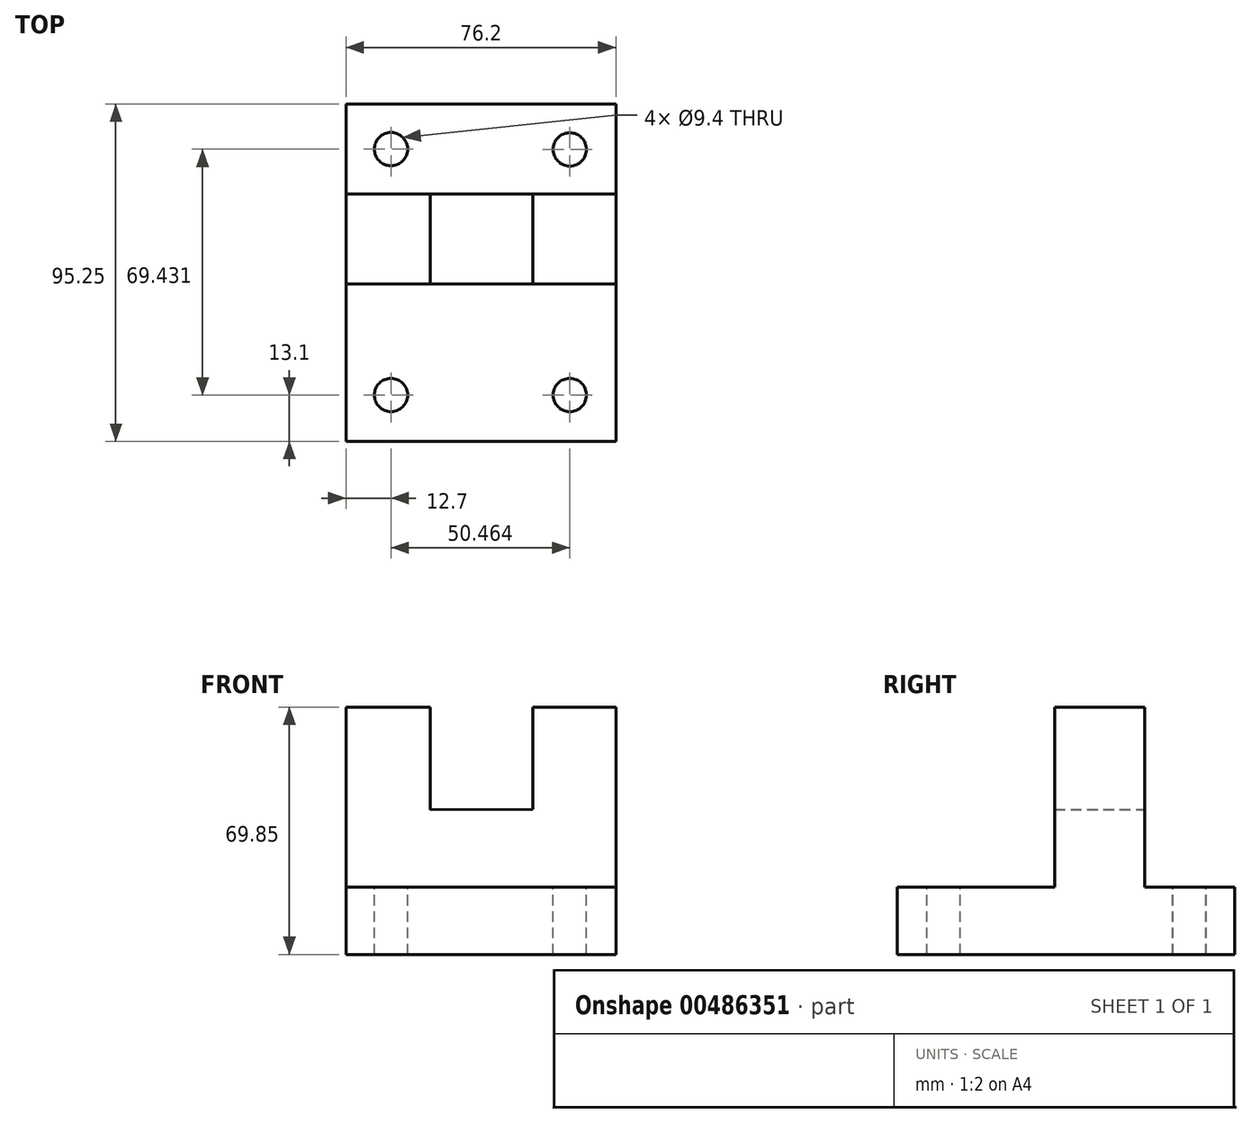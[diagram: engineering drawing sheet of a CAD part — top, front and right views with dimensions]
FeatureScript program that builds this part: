
annotation { "Feature Type Name" : "Feature", "Feature Type Description" : "" }
export const myFeature = defineFeature(function(context is Context, id is Id, definition is map)
    precondition{}
    {
        {
            var Q0;
            Q0=qCreatedBy(makeId("Right.planeOp"),FACE);
            var sketch = newSketch(context, id + "F0", { "sketchPlane" : qUnion([Q0])});
            skLineSegment(sketch, "E0", {"start": v(40.84, -32.67) * mm, "end": v(-54.41, -32.67) * mm});
            skLineSegment(sketch, "E1", {"start": v(40.84, -32.67) * mm, "end": v(40.84, -13.62) * mm});
            skLineSegment(sketch, "E2", {"start": v(-54.41, -32.67) * mm, "end": v(-54.41, -13.62) * mm});
            skLineSegment(sketch, "E3", {"start": v(-54.41, -13.62) * mm, "end": v(-9.96, -13.62) * mm});
            skLineSegment(sketch, "E4", {"start": v(-9.96, -13.62) * mm, "end": v(-9.96, 37.18) * mm});
            skLineSegment(sketch, "E5", {"start": v(-9.96, 37.18) * mm, "end": v(15.44, 37.18) * mm});
            skLineSegment(sketch, "E6", {"start": v(40.84, -13.62) * mm, "end": v(15.44, -13.62) * mm});
            skLineSegment(sketch, "E7", {"start": v(15.44, -13.62) * mm, "end": v(15.44, 37.18) * mm});
            skSolve(sketch);
        }
        {
            var Q0;
            Q0=makeQuery(id+"F0.imprint","IMPRINT",FACE,{"disambiguationData":[TD([[makeQuery(id+"F0.imprint","IMPRINT",EDGE,{"derivedFrom":sQuery(id+"F0.wireOp",EDGE,"E0")}),-1.0]])]});
            extrude(context, id + "F1", {"entities" : qUnion([Q0]), "depth" : 76.2 * mm, "offsetDistance" : 25.4 * mm});
        }
        {
            var Q0;
            Q0=qCreatedBy(makeId("Front.planeOp"),FACE);
            var sketch = newSketch(context, id + "F2", { "sketchPlane" : qUnion([Q0])});
            skLineSegment(sketch, "E8", {"start": v(52.71, 36.94) * mm, "end": v(52.71, 8.36) * mm});
            skLineSegment(sketch, "E9", {"start": v(23.83, 36.77) * mm, "end": v(23.83, 8.2) * mm});
            skLineSegment(sketch, "E10", {"start": v(23.83, 8.2) * mm, "end": v(52.71, 8.36) * mm});
            skPoint(sketch, "E11.start.orphan", {"position": v(0, 36.77) * mm});
            skLineSegment(sketch, "E12", {"start": v(23.83, 36.77) * mm, "end": v(23.83, 49.71) * mm});
            skLineSegment(sketch, "E13", {"start": v(23.83, 49.71) * mm, "end": v(52.71, 49.71) * mm});
            skLineSegment(sketch, "E14", {"start": v(52.71, 49.71) * mm, "end": v(52.71, 36.94) * mm});
            skSolve(sketch);
        }
        {
            var Q0;
            Q0=makeQuery(id+"F2.imprint","IMPRINT",FACE,{"disambiguationData":[TD([[makeQuery(id+"F2.imprint","IMPRINT",EDGE,{"derivedFrom":sQuery(id+"F2.wireOp",EDGE,"E8")}),-1.0]])]});
            var Q1;
            Q1=makeQuery(id+"F2.imprint","IMPRINT",FACE,{"disambiguationData":[TD([[makeQuery(id+"F2.imprint","IMPRINT",EDGE,{"derivedFrom":sQuery(id+"F2.wireOp",EDGE,"E8")}),-1.0]])]});
            extrude(context, id + "F3", {"entities" : qUnion([Q0, Q1]), "operationType" : NewBodyOperationType.REMOVE, "endBound" : BoundingType.THROUGH_ALL, "depth" : 25.4 * mm, "offsetDistance" : 25.4 * mm, "hasSecondDirection" : true, "secondDirectionOppositeDirection" : true, "secondDirectionDepth" : 50.8 * mm});
        }
        {
            var Q0;
            Q0=qCreatedBy(makeId("Top.planeOp"),FACE);
            var sketch = newSketch(context, id + "F4", { "sketchPlane" : qUnion([Q0])});
            skCircle(sketch, "E15", {"center": v(63.16, -41.31) * mm, "radius": 4.7 * mm});
            skPoint(sketch, "E16.end.orphan", {"position": v(75.86, -41.31) * mm});
            skPoint(sketch, "E17.end.orphan", {"position": v(63.16, -54.01) * mm});
            skCircle(sketch, "E18", {"center": v(12.7, -41.31) * mm, "radius": 4.7 * mm});
            skPoint(sketch, "E19.end.orphan", {"position": v(0, -41.31) * mm});
            skPoint(sketch, "E20.end.orphan", {"position": v(12.7, -54.01) * mm});
            skPoint(sketch, "E20.start.orphan", {"position": v(0, -54.01) * mm});
            skLineSegment(sketch, "E21", {"start": v(0, 40.82) * mm, "end": v(0, 28.12) * mm});
            skCircle(sketch, "E22", {"center": v(12.7, 28.12) * mm, "radius": 4.7 * mm});
            skPoint(sketch, "E23.start.orphan", {"position": v(12.7, 40.82) * mm});
            skLineSegment(sketch, "E24", {"start": v(76.2, 40.74) * mm, "end": v(76.2, 28.04) * mm});
            skCircle(sketch, "E25", {"center": v(63.16, 28.04) * mm, "radius": 4.7 * mm});
            skSolve(sketch);
        }
        {
            var Q0;
            Q0=makeQuery(id+"F4.imprint","IMPRINT",FACE,{"disambiguationData":[TD([[makeQuery(id+"F4.imprint","IMPRINT",EDGE,{"derivedFrom":sQuery(id+"F4.wireOp",EDGE,"E22")}),1.0]])]});
            var Q1;
            Q1=makeQuery(id+"F4.imprint","IMPRINT",FACE,{"disambiguationData":[TD([[makeQuery(id+"F4.imprint","IMPRINT",EDGE,{"derivedFrom":sQuery(id+"F4.wireOp",EDGE,"E25")}),1.0]])]});
            var Q2;
            Q2=makeQuery(id+"F4.imprint","IMPRINT",FACE,{"disambiguationData":[TD([[makeQuery(id+"F4.imprint","IMPRINT",EDGE,{"derivedFrom":sQuery(id+"F4.wireOp",EDGE,"E15")}),1.0]])]});
            var Q3;
            Q3=makeQuery(id+"F4.imprint","IMPRINT",FACE,{"disambiguationData":[TD([[makeQuery(id+"F4.imprint","IMPRINT",EDGE,{"derivedFrom":sQuery(id+"F4.wireOp",EDGE,"E18")}),1.0]])]});
            extrude(context, id + "F5", {"entities" : qUnion([Q0, Q1, Q2, Q3]), "operationType" : NewBodyOperationType.REMOVE, "endBound" : BoundingType.THROUGH_ALL, "oppositeDirection" : true, "depth" : 25.4 * mm, "offsetDistance" : 25.4 * mm});
        }
    });
